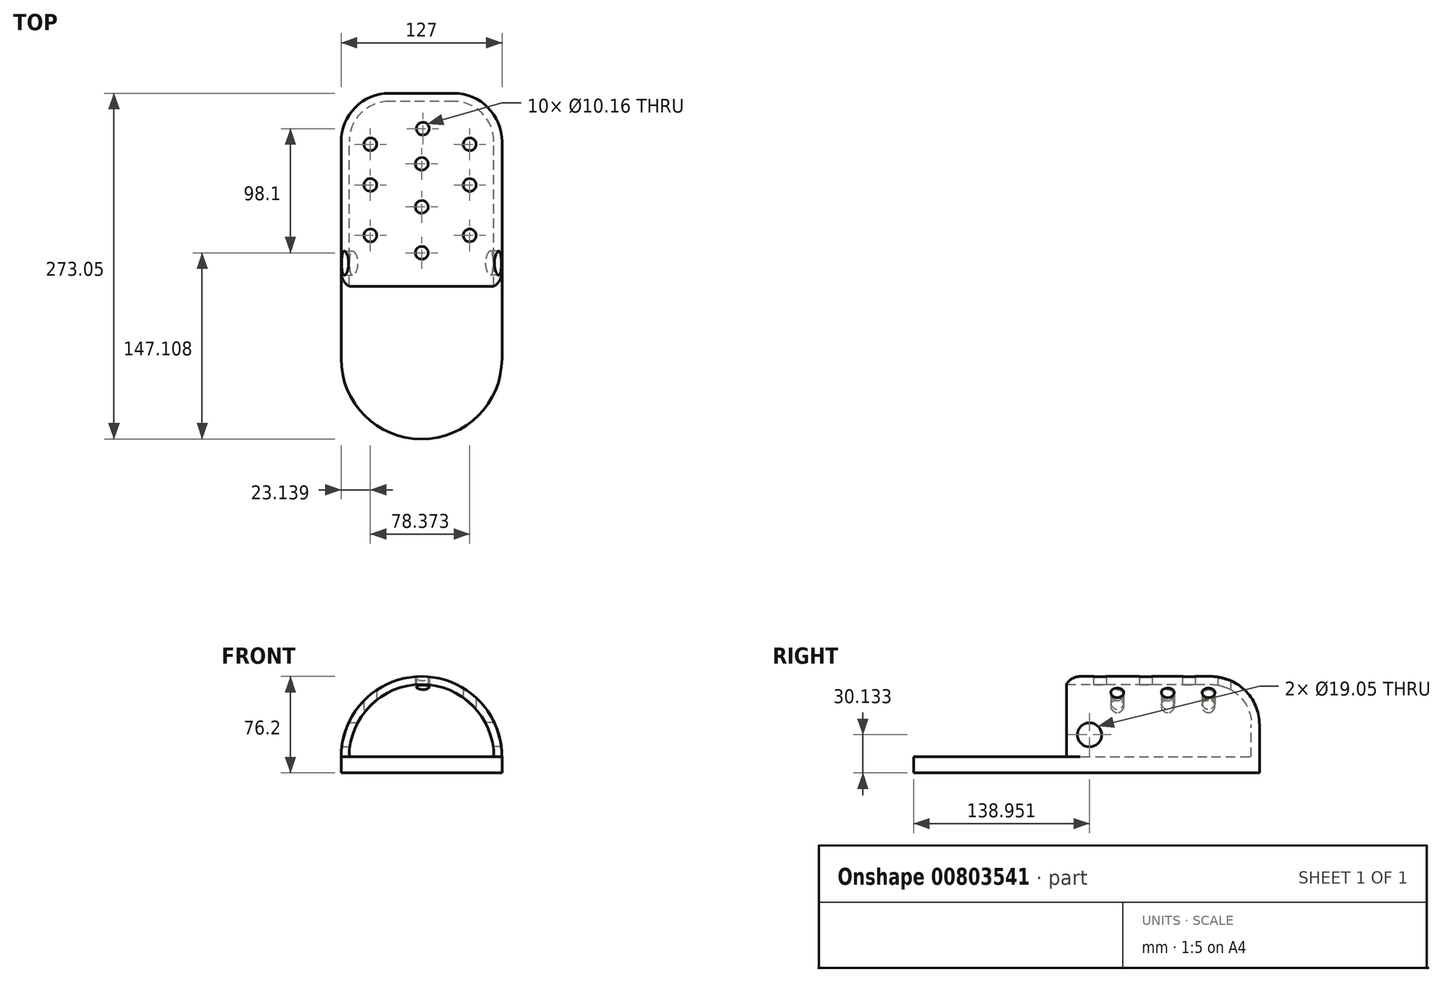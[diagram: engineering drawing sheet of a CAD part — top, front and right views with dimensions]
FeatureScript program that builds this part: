
annotation { "Feature Type Name" : "Feature", "Feature Type Description" : "" }
export const myFeature = defineFeature(function(context is Context, id is Id, definition is map)
    precondition{}
    {
        {
            var Q0;
            Q0=qCreatedBy(makeId("Front.planeOp"),FACE);
            var sketch = newSketch(context, id + "F0", { "sketchPlane" : qUnion([Q0])});
            skArc(sketch, "E0", {"start": v(62.5, 0) * mm, "mid": v(-1, 63.5) * mm, "end": v(-64.5, 0) * mm});
            skLineSegment(sketch, "E1", {"start": v(-64.5, 0) * mm, "end": v(62.5, 0) * mm});
            skLineSegment(sketch, "E2", {"start": v(62.5, 0) * mm, "end": v(62.5, -12.7) * mm});
            skLineSegment(sketch, "E3", {"start": v(62.5, -12.7) * mm, "end": v(-64.5, -12.7) * mm});
            skLineSegment(sketch, "E4", {"start": v(-64.5, -12.7) * mm, "end": v(-64.5, 0) * mm});
            skSolve(sketch);
        }
        {
            var Q0;
            Q0=makeQuery(id+"F0.imprint","IMPRINT",FACE,{"disambiguationData":[TD([[makeQuery(id+"F0.imprint","IMPRINT",EDGE,{"derivedFrom":sQuery(id+"F0.wireOp",EDGE,"E1")}),-1.0]])]});
            extrude(context, id + "F1", {"entities" : qUnion([Q0]), "depth" : 273.05 * mm, "offsetDistance" : 25.4 * mm});
        }
        {
            var Q0;
            Q0=makeQuery(id+"F0.imprint","IMPRINT",FACE,{"disambiguationData":[TD([[makeQuery(id+"F0.imprint","IMPRINT",EDGE,{"derivedFrom":sQuery(id+"F0.wireOp",EDGE,"E0")}),1.0]])]});
            extrude(context, id + "F2", {"entities" : qUnion([Q0]), "operationType" : NewBodyOperationType.ADD, "depth" : 152.4 * mm, "offsetDistance" : 25.4 * mm});
        }
        {
            var Q0;
            Q0=makeQuery(id+"F1.opExtrude","CAP_EDGE",EDGE,{"disambiguationData":[OSD([sQuery(id+"F0.wireOp",EDGE,"E4")])],"isStart":false});
            var Q1;
            Q1=makeQuery(id+"F1.opExtrude","CAP_EDGE",EDGE,{"disambiguationData":[OSD([sQuery(id+"F0.wireOp",EDGE,"E2")])],"isStart":false});
            fillet(context, id + "F3", {"entities" : qUnion([Q0, Q1]), "radius" : 63.5 * mm, "tangentPropagation" : true, "allowEdgeOverflow" : false});
        }
        {
            var Q0;
            Q0=makeQuery(id+"F2.opExtrude","CAP_EDGE",EDGE,{"disambiguationData":[OSD([sQuery(id+"F0.wireOp",EDGE,"E0")])],"isStart":true});
            fillet(context, id + "F4", {"entities" : qUnion([Q0]), "radius" : 38.1 * mm, "tangentPropagation" : true, "allowEdgeOverflow" : false});
        }
        {
            var Q0;
            Q0=makeQuery(id+"F2.opExtrude","CAP_FACE",FACE,{"disambiguationData":[OSD([sQuery(id+"F0.wireOp",EDGE,"E0"),sQuery(id+"F0.wireOp",EDGE,"E1")])],"isStart":false});
            shell(context, id + "F5", {"entities" : qUnion([Q0]), "thickness" : 6.35 * mm});
        }
        {
            var Q0;
            Q0=makeQuery(id+"F5.opShell","OFFSET_FACE",FACE,{"disambiguationData":[OSD([sQuery(id+"F0.wireOp",EDGE,"E3")])]});
            var Q1;
            Q1=makeQuery(id+"F1.opExtrude","SWEPT_FACE",FACE,{"disambiguationData":[OSD([sQuery(id+"F0.wireOp",EDGE,"E1")])]});
            extrude(context, id + "F6", {"entities" : qUnion([Q0]), "operationType" : NewBodyOperationType.ADD, "endBound" : BoundingType.UP_TO_SURFACE, "depth" : 25.4 * mm, "endBoundEntityFace" : qUnion([Q1]), "offsetDistance" : 25.4 * mm});
        }
        {
            var Q0;
            {var subQ0=sQuery(id+"F0.wireOp",EDGE,"E1");Q0=makeQuery(id+"F6.boolean.opBoolean","MERGE",FACE,{"derivedFrom":[makeQuery(id+"F1.opExtrude","SWEPT_FACE",FACE,{"disambiguationData":[OSD([subQ0])]}),makeQuery(id+"F6.opExtrude","CAP_FACE",FACE,{"disambiguationData":[OSD([subQ0])],"isStart":false})]});}
            var sketch = newSketch(context, id + "F7", { "sketchPlane" : qUnion([Q0])});
            skCircle(sketch, "E5", {"center": v(0, -27.84) * mm, "radius": 5.08 * mm});
            skCircle(sketch, "E6", {"center": v(-0.84, -55.68) * mm, "radius": 5.08 * mm});
            skCircle(sketch, "E7", {"center": v(-0.84, -89.7) * mm, "radius": 5.08 * mm});
            skCircle(sketch, "E8", {"center": v(37.02, -112.2) * mm, "radius": 5.08 * mm});
            skCircle(sketch, "E9", {"center": v(37.02, -72.37) * mm, "radius": 5.08 * mm});
            skCircle(sketch, "E10", {"center": v(37.02, -40.22) * mm, "radius": 5.08 * mm});
            skCircle(sketch, "E11", {"center": v(-41.35, -40.22) * mm, "radius": 5.08 * mm});
            skCircle(sketch, "E12", {"center": v(-41.35, -72.37) * mm, "radius": 5.08 * mm});
            skCircle(sketch, "E13", {"center": v(-41.35, -112.2) * mm, "radius": 5.08 * mm});
            skCircle(sketch, "E14", {"center": v(-0.84, -125.94) * mm, "radius": 5.08 * mm});
            skSolve(sketch);
        }
        {
            var Q0;
            Q0 = qSketchRegion(id + "F7", true);
            var Q1;
            Q1=makeQuery(id+"F2.opExtrude","SWEPT_FACE",FACE,{"disambiguationData":[OSD([sQuery(id+"F0.wireOp",EDGE,"E0")])]});
            extrude(context, id + "F8", {"entities" : qUnion([Q0]), "operationType" : NewBodyOperationType.REMOVE, "endBound" : BoundingType.UP_TO_SURFACE, "depth" : 25.4 * mm, "endBoundEntityFace" : qUnion([Q1]), "offsetDistance" : 25.4 * mm});
        }
        {
            var Q0;
            Q0=qCreatedBy(makeId("Right.planeOp"),FACE);
            var sketch = newSketch(context, id + "F9", { "sketchPlane" : qUnion([Q0])});
            skCircle(sketch, "E15", {"center": v(-134.1, 17.43) * mm, "radius": 9.53 * mm});
            skSolve(sketch);
        }
        {
            var Q0;
            Q0 = qSketchRegion(id + "F9", true);
            extrude(context, id + "F10", {"entities" : qUnion([Q0]), "operationType" : NewBodyOperationType.REMOVE, "endBound" : BoundingType.THROUGH_ALL, "oppositeDirection" : true, "depth" : 25.4 * mm, "offsetDistance" : 25.4 * mm});
        }
        {
            var Q0;
            Q0 = qSketchRegion(id + "F9", true);
            extrude(context, id + "F11", {"entities" : qUnion([Q0]), "operationType" : NewBodyOperationType.REMOVE, "endBound" : BoundingType.THROUGH_ALL, "depth" : 25.4 * mm, "offsetDistance" : 25.4 * mm});
        }
        {
            var Q0;
            Q0=makeQuery(id+"F2.opExtrude","CAP_EDGE",EDGE,{"disambiguationData":[OSD([sQuery(id+"F0.wireOp",EDGE,"E0")])],"isStart":false});
            fillet(context, id + "F12", {"entities" : qUnion([Q0]), "radius" : 12.7 * mm, "tangentPropagation" : true, "allowEdgeOverflow" : false});
        }
    });
